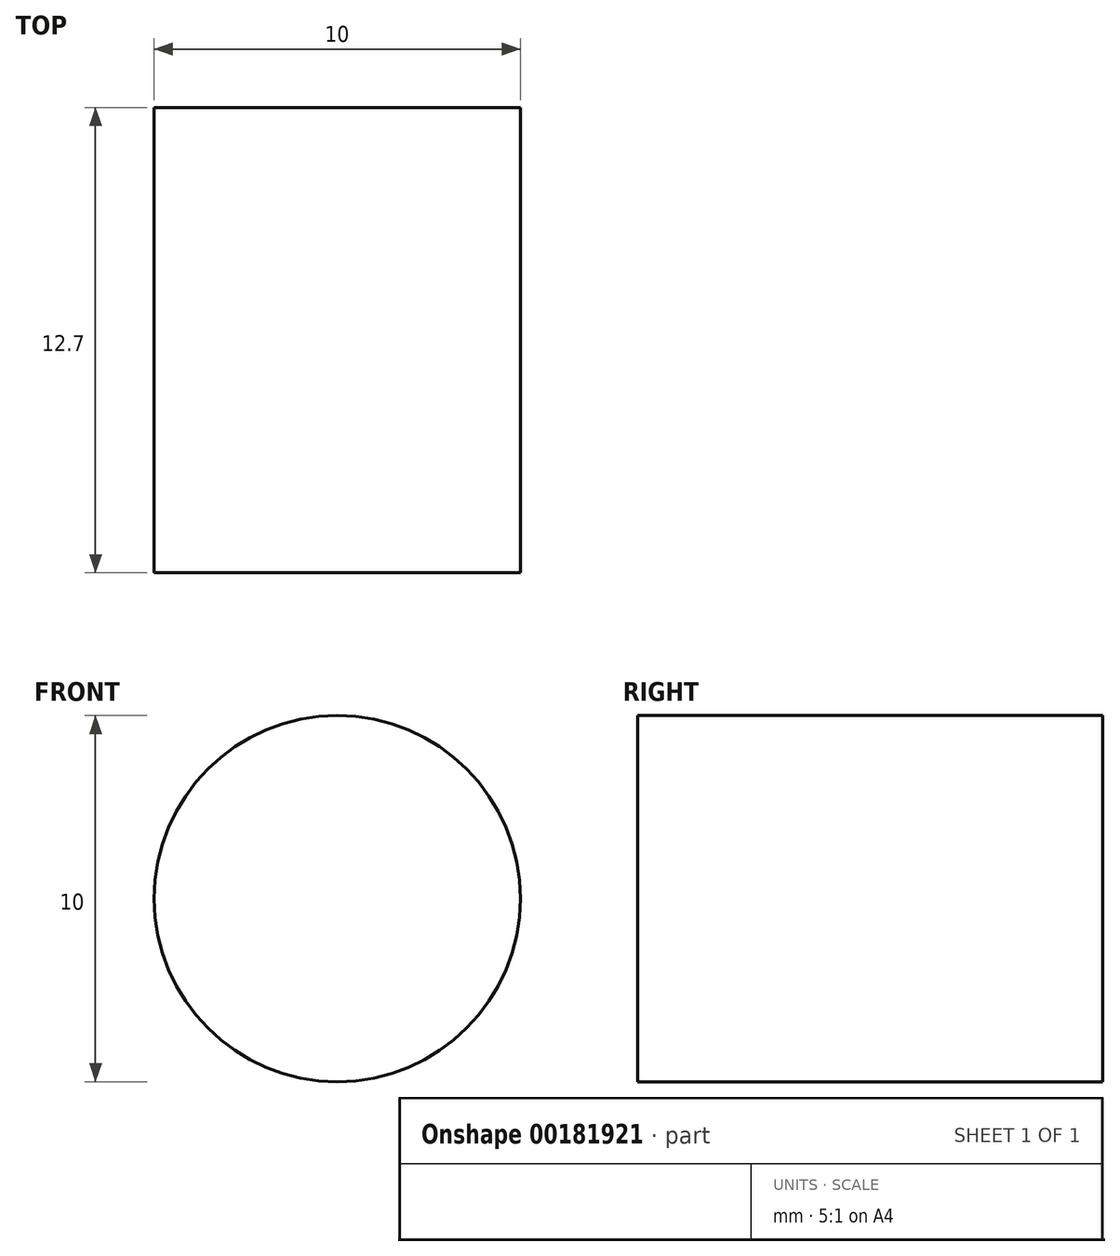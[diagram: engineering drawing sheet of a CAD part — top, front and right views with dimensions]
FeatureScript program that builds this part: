
annotation { "Feature Type Name" : "Feature", "Feature Type Description" : "" }
export const myFeature = defineFeature(function(context is Context, id is Id, definition is map)
    precondition{}
    {
        {
            var Q0;
            Q0=qCreatedBy(makeId("Front.planeOp"),FACE);
            var sketch = newSketch(context, id + "F0", { "sketchPlane" : qUnion([Q0])});
            skCircle(sketch, "E0", {"center": v(0, 0) * mm, "radius": 5 * mm});
            skSolve(sketch);
        }
        {
            var Q0;
            Q0=sQuery(id+"F0.wireOp",EDGE,"E0");
            extrude(context, id + "F1", {"bodyType" : ToolBodyType.SURFACE, "surfaceEntities" : qUnion([Q0]), "depth" : 12.7 * mm});
        }
    });
